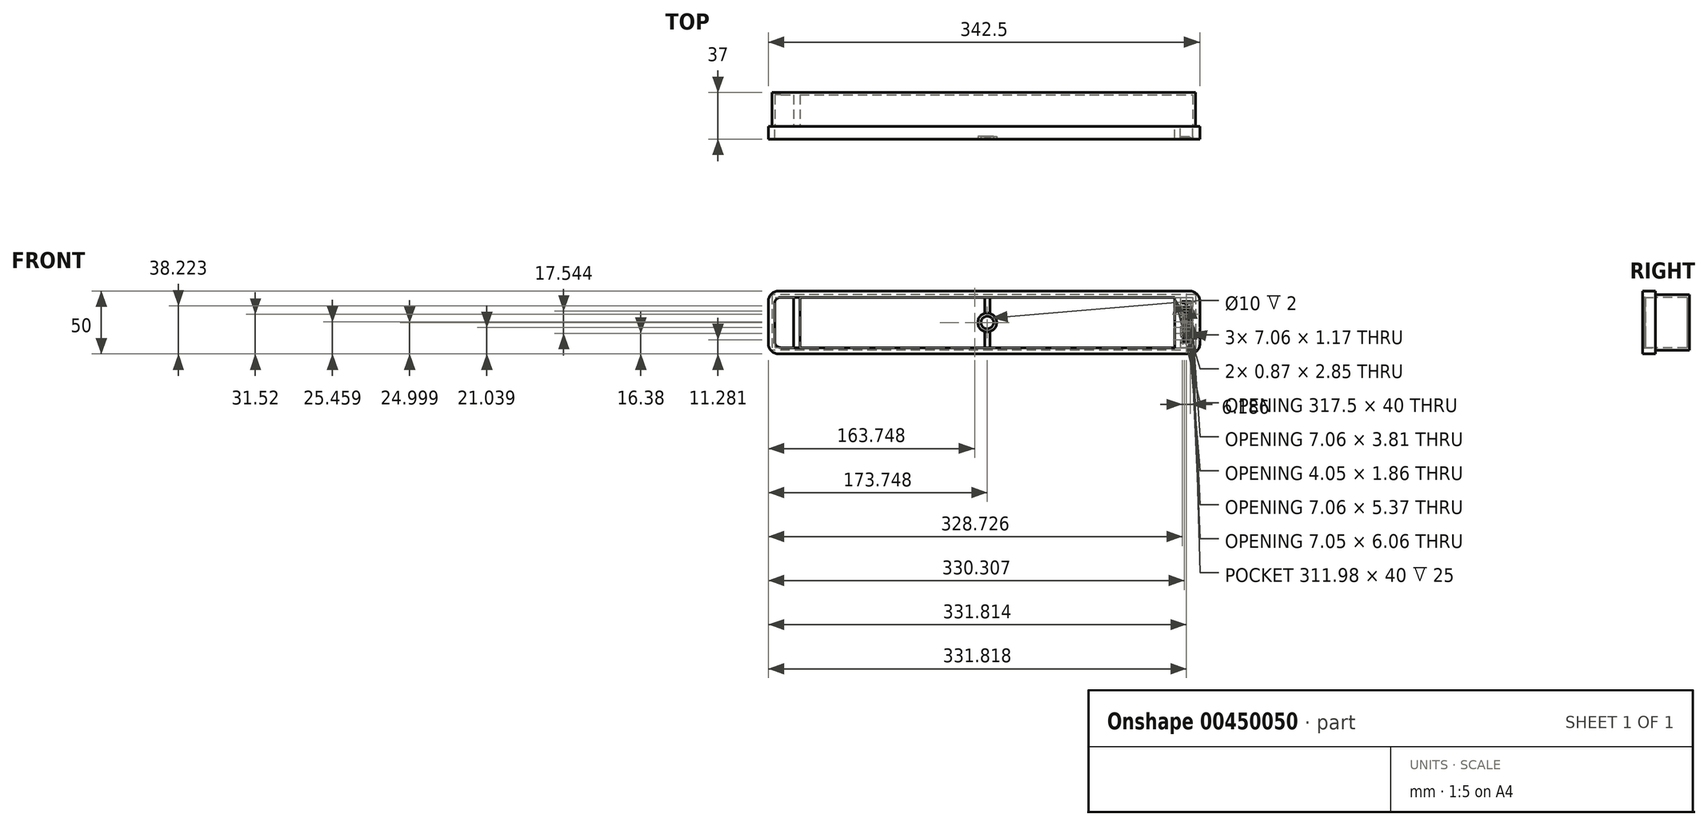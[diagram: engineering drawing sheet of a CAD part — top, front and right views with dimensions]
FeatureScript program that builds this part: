
annotation { "Feature Type Name" : "Feature", "Feature Type Description" : "" }
export const myFeature = defineFeature(function(context is Context, id is Id, definition is map)
    precondition{}
    {
        {
            var Q0;
            Q0=qCreatedBy(makeId("Front.planeOp"),FACE);
            var sketch = newSketch(context, id + "F0", { "sketchPlane" : qUnion([Q0])});
            skLineSegment(sketch, "E0.bottom", {"start": v(-305.43, 21.95) * mm, "end": v(20.67, 21.95) * mm});
            skLineSegment(sketch, "E0.top", {"start": v(-305.43, -28.05) * mm, "end": v(20.67, -28.05) * mm});
            skLineSegment(sketch, "E0.left", {"start": v(-313.63, 13.75) * mm, "end": v(-313.63, -19.85) * mm});
            skLineSegment(sketch, "E0.right", {"start": v(28.87, 13.75) * mm, "end": v(28.87, -19.85) * mm});
            skLineSegment(sketch, "E1.bottom", {"start": v(-303.63, 16.95) * mm, "end": v(8.87, 16.95) * mm});
            skLineSegment(sketch, "E1.top", {"start": v(-303.63, -23.05) * mm, "end": v(8.87, -23.05) * mm});
            skLineSegment(sketch, "E1.left", {"start": v(-308.63, 11.95) * mm, "end": v(-308.63, -18.05) * mm});
            skLineSegment(sketch, "E1.right", {"start": v(8.87, 16.95) * mm, "end": v(8.87, -23.05) * mm});
            skPoint(sketch, "E2.visualSharp", {"position": v(-308.63, 16.95) * mm});
            skArc(sketch, "E2.filletArc", {"start": v(-303.63, 16.95) * mm, "mid": v(-307.17, 15.48) * mm, "end": v(-308.63, 11.95) * mm});
            skPoint(sketch, "E3.visualSharp", {"position": v(-308.63, -23.05) * mm});
            skArc(sketch, "E3.filletArc", {"start": v(-308.63, -18.05) * mm, "mid": v(-307.17, -21.59) * mm, "end": v(-303.63, -23.05) * mm});
            skPoint(sketch, "E4.visualSharp", {"position": v(-313.63, -28.05) * mm});
            skArc(sketch, "E4.filletArc", {"start": v(-313.63, -19.85) * mm, "mid": v(-311.23, -25.65) * mm, "end": v(-305.43, -28.05) * mm});
            skPoint(sketch, "E5.visualSharp", {"position": v(-313.63, 21.95) * mm});
            skArc(sketch, "E5.filletArc", {"start": v(-305.43, 21.95) * mm, "mid": v(-311.23, 19.55) * mm, "end": v(-313.63, 13.75) * mm});
            skPoint(sketch, "E6.visualSharp", {"position": v(28.87, 21.95) * mm});
            skArc(sketch, "E6.filletArc", {"start": v(28.87, 13.75) * mm, "mid": v(26.47, 19.55) * mm, "end": v(20.67, 21.95) * mm});
            skPoint(sketch, "E7.visualSharp", {"position": v(28.87, -28.05) * mm});
            skArc(sketch, "E7.filletArc", {"start": v(20.67, -28.05) * mm, "mid": v(26.47, -25.65) * mm, "end": v(28.87, -19.85) * mm});
            skLineSegment(sketch, "E8.bottom", {"start": v(-293.63, 16.95) * mm, "end": v(-288.63, 16.95) * mm});
            skLineSegment(sketch, "E8.top", {"start": v(-293.63, -23.05) * mm, "end": v(-288.63, -23.05) * mm});
            skLineSegment(sketch, "E8.left", {"start": v(-293.63, 16.95) * mm, "end": v(-293.63, -23.05) * mm});
            skLineSegment(sketch, "E8.right", {"start": v(-288.63, 16.95) * mm, "end": v(-288.63, -23.05) * mm});
            skSolve(sketch);
        }
        {
            var Q0;
            Q0=makeQuery(id+"F0.imprint","IMPRINT",FACE,{"disambiguationData":[TD([[makeQuery(id+"F0.imprint","IMPRINT",EDGE,{"derivedFrom":sQuery(id+"F0.wireOp",EDGE,"E0.bottom")}),-1.0]])]});
            var Q1;
            Q1=makeQuery(id+"F0.imprint","IMPRINT",FACE,{"disambiguationData":[TD([[makeQuery(id+"F0.imprint","IMPRINT",EDGE,{"derivedFrom":sQuery(id+"F0.wireOp",EDGE,"E8.bottom")}),-1.0]])]});
            extrude(context, id + "F1", {"entities" : qUnion([Q0, Q1]), "depth" : 10 * mm});
        }
        {
            var Q0;
            Q0=makeQuery(id+"F1.opExtrude","CAP_FACE",FACE,{"disambiguationData":[OSD([sQuery(id+"F0.wireOp",EDGE,"E0.bottom"),sQuery(id+"F0.wireOp",EDGE,"E0.top"),sQuery(id+"F0.wireOp",EDGE,"E0.left"),sQuery(id+"F0.wireOp",EDGE,"E0.right"),sQuery(id+"F0.wireOp",EDGE,"E1.bottom"),sQuery(id+"F0.wireOp",EDGE,"E1.top"),sQuery(id+"F0.wireOp",EDGE,"E1.left"),sQuery(id+"F0.wireOp",EDGE,"E1.right"),sQuery(id+"F0.wireOp",EDGE,"zvlTqXnN-NSDQ-JKbX-Zw8z-ZxoE4PYBJVqr.bottom"),sQuery(id+"F0.wireOp",EDGE,"zvlTqXnN-NSDQ-JKbX-Zw8z-ZxoE4PYBJVqr.top"),sQuery(id+"F0.wireOp",EDGE,"zvlTqXnN-NSDQ-JKbX-Zw8z-ZxoE4PYBJVqr.left"),sQuery(id+"F0.wireOp",EDGE,"zvlTqXnN-NSDQ-JKbX-Zw8z-ZxoE4PYBJVqr.right"),sQuery(id+"F0.wireOp",EDGE,"uq8vt4s5-scxk-EfTv-IjQb-mOJCmNg2LhQu.bottom"),sQuery(id+"F0.wireOp",EDGE,"uq8vt4s5-scxk-EfTv-IjQb-mOJCmNg2LhQu.top"),sQuery(id+"F0.wireOp",EDGE,"uq8vt4s5-scxk-EfTv-IjQb-mOJCmNg2LhQu.left"),sQuery(id+"F0.wireOp",EDGE,"uq8vt4s5-scxk-EfTv-IjQb-mOJCmNg2LhQu.right"),sQuery(id+"F0.wireOp",EDGE,"y3TFfong-PjZo-lhFq-87m7-LgytcNZYgRy1.bottom"),sQuery(id+"F0.wireOp",EDGE,"y3TFfong-PjZo-lhFq-87m7-LgytcNZYgRy1.top"),sQuery(id+"F0.wireOp",EDGE,"y3TFfong-PjZo-lhFq-87m7-LgytcNZYgRy1.left"),sQuery(id+"F0.wireOp",EDGE,"y3TFfong-PjZo-lhFq-87m7-LgytcNZYgRy1.right"),sQuery(id+"F0.wireOp",EDGE,"Yr4FkV4U-5VVj-icSQ-0UOe-qvVzSsorRwRa.bottom"),sQuery(id+"F0.wireOp",EDGE,"Yr4FkV4U-5VVj-icSQ-0UOe-qvVzSsorRwRa.top"),sQuery(id+"F0.wireOp",EDGE,"Yr4FkV4U-5VVj-icSQ-0UOe-qvVzSsorRwRa.left"),sQuery(id+"F0.wireOp",EDGE,"Yr4FkV4U-5VVj-icSQ-0UOe-qvVzSsorRwRa.right")])],"isStart":false});
            var sketch = newSketch(context, id + "F2", { "sketchPlane" : qUnion([Q0])});
            skText(sketch, "E9", { "text": "HESTIA", "fontName": "AllertaStencil-Regular.ttf"});
            const initialGuessF2  = {"E9": [0.01466, 0.01454, 0, -1, 0.00706]};
            skSetInitialGuess(sketch, initialGuessF2);
            skSolve(sketch);
        }
        {
            var Q0;
            Q0 = qSketchRegion(id + "F2", true);
            extrude(context, id + "F3", {"entities" : qUnion([Q0]), "operationType" : NewBodyOperationType.REMOVE, "oppositeDirection" : true, "depth" : 5 * mm});
        }
        {
            var Q0;
            Q0=makeQuery(id+"F1.opExtrude","CAP_FACE",FACE,{"disambiguationData":[OSD([sQuery(id+"F0.wireOp",EDGE,"E0.bottom"),sQuery(id+"F0.wireOp",EDGE,"E0.top"),sQuery(id+"F0.wireOp",EDGE,"E0.left"),sQuery(id+"F0.wireOp",EDGE,"E0.right"),sQuery(id+"F0.wireOp",EDGE,"E1.bottom"),sQuery(id+"F0.wireOp",EDGE,"E1.top"),sQuery(id+"F0.wireOp",EDGE,"E1.left"),sQuery(id+"F0.wireOp",EDGE,"E1.right"),sQuery(id+"F0.wireOp",EDGE,"E2.filletArc"),sQuery(id+"F0.wireOp",EDGE,"E3.filletArc"),sQuery(id+"F0.wireOp",EDGE,"E4.filletArc"),sQuery(id+"F0.wireOp",EDGE,"E5.filletArc"),sQuery(id+"F0.wireOp",EDGE,"E6.filletArc"),sQuery(id+"F0.wireOp",EDGE,"E7.filletArc"),sQuery(id+"F0.wireOp",EDGE,"E8.left"),sQuery(id+"F0.wireOp",EDGE,"E8.right")])],"isStart":false});
            var sketch = newSketch(context, id + "F4", { "sketchPlane" : qUnion([Q0])});
            skCircle(sketch, "E10", {"center": v(-139.88, -3.05) * mm, "radius": 5 * mm});
            skPoint(sketch, "E10.centerSnap0", {"position": v(-288.63, -3.05) * mm});
            skLineSegment(sketch, "E11", {"start": v(-288.63, -3.05) * mm, "end": v(8.87, -3.05) * mm, "construction": true});
            skCircle(sketch, "E12", {"center": v(-139.88, -3.05) * mm, "radius": 7.5 * mm});
            skSolve(sketch);
        }
        {
            var Q0;
            Q0=makeQuery(id+"F4.imprint","IMPRINT",FACE,{"disambiguationData":[TD([[makeQuery(id+"F4.imprint","IMPRINT",EDGE,{"derivedFrom":sQuery(id+"F4.wireOp",EDGE,"E10")}),-1.0]])]});
            extrude(context, id + "F5", {"entities" : qUnion([Q0]), "operationType" : NewBodyOperationType.ADD, "oppositeDirection" : true, "depth" : 2 * mm});
        }
        {
            var Q0;
            Q0=makeQuery(id+"F5.opExtrude","CAP_FACE",FACE,{"disambiguationData":[OSD([sQuery(id+"F4.wireOp",EDGE,"E10"),sQuery(id+"F4.wireOp",EDGE,"E12")])],"isStart":false});
            var sketch = newSketch(context, id + "F6", { "sketchPlane" : qUnion([Q0])});
            skLineSegment(sketch, "E13.bottom", {"start": v(141.89, -8.94) * mm, "end": v(137.72, -8.94) * mm});
            skLineSegment(sketch, "E13.top", {"start": v(141.89, -23.04) * mm, "end": v(137.72, -23.04) * mm});
            skLineSegment(sketch, "E13.left", {"start": v(141.89, -8.94) * mm, "end": v(141.89, -23.04) * mm});
            skLineSegment(sketch, "E13.right", {"start": v(137.72, -8.94) * mm, "end": v(137.72, -23.04) * mm});
            skLineSegment(sketch, "E14.bottom", {"start": v(141.89, 3.14) * mm, "end": v(137.72, 3.14) * mm});
            skLineSegment(sketch, "E14.top", {"start": v(141.89, 16.95) * mm, "end": v(137.72, 16.95) * mm});
            skLineSegment(sketch, "E14.left", {"start": v(141.89, 3.14) * mm, "end": v(141.89, 16.95) * mm});
            skLineSegment(sketch, "E14.right", {"start": v(137.72, 3.14) * mm, "end": v(137.72, 16.95) * mm});
            skSolve(sketch);
        }
        {
            var Q0;
            {var subQ0=sQuery(id+"F6.wireOp",EDGE,"E14.top");Q0=makeQuery(id+"F6.imprint","IMPRINT",FACE,{"disambiguationData":[TD([[makeQuery(id+"F6.imprint","IMPRINT",EDGE,{"derivedFrom":subQ0}),1.0]])]});}
            var Q1;
            {var subQ0=sQuery(id+"F6.wireOp",EDGE,"E14.bottom");Q1=makeQuery(id+"F6.imprint","IMPRINT",FACE,{"disambiguationData":[TD([[makeQuery(id+"F6.imprint","IMPRINT",EDGE,{"derivedFrom":subQ0}),-1.0]])]});}
            var Q2;
            {var subQ0=sQuery(id+"F6.wireOp",EDGE,"E13.bottom");Q2=makeQuery(id+"F6.imprint","IMPRINT",FACE,{"disambiguationData":[TD([[makeQuery(id+"F6.imprint","IMPRINT",EDGE,{"derivedFrom":subQ0}),1.0]])]});}
            var Q3;
            {var subQ0=sQuery(id+"F6.wireOp",EDGE,"E13.top");Q3=makeQuery(id+"F6.imprint","IMPRINT",FACE,{"disambiguationData":[TD([[makeQuery(id+"F6.imprint","IMPRINT",EDGE,{"derivedFrom":subQ0}),-1.0]])]});}
            extrude(context, id + "F7", {"entities" : qUnion([Q0, Q1, Q2, Q3]), "operationType" : NewBodyOperationType.ADD, "oppositeDirection" : true, "depth" : 1 * mm});
        }
        {
            var Q0;
            Q0=makeQuery(id+"F1.opExtrude","CAP_FACE",FACE,{"disambiguationData":[OSD([sQuery(id+"F0.wireOp",EDGE,"E0.bottom"),sQuery(id+"F0.wireOp",EDGE,"E0.top"),sQuery(id+"F0.wireOp",EDGE,"E0.left"),sQuery(id+"F0.wireOp",EDGE,"E0.right"),sQuery(id+"F0.wireOp",EDGE,"E1.bottom"),sQuery(id+"F0.wireOp",EDGE,"E1.top"),sQuery(id+"F0.wireOp",EDGE,"E1.left"),sQuery(id+"F0.wireOp",EDGE,"E1.right"),sQuery(id+"F0.wireOp",EDGE,"E2.filletArc"),sQuery(id+"F0.wireOp",EDGE,"E3.filletArc"),sQuery(id+"F0.wireOp",EDGE,"E4.filletArc"),sQuery(id+"F0.wireOp",EDGE,"E5.filletArc"),sQuery(id+"F0.wireOp",EDGE,"E6.filletArc"),sQuery(id+"F0.wireOp",EDGE,"E7.filletArc"),sQuery(id+"F0.wireOp",EDGE,"E8.left"),sQuery(id+"F0.wireOp",EDGE,"E8.right")])],"isStart":true});
            var sketch = newSketch(context, id + "F8", { "sketchPlane" : qUnion([Q0])});
            skLineSegment(sketch, "E15.bottom", {"start": v(-13.33, 16.95) * mm, "end": v(-23.35, 16.95) * mm});
            skLineSegment(sketch, "E15.top", {"start": v(-13.33, -22.98) * mm, "end": v(-23.35, -22.98) * mm});
            skLineSegment(sketch, "E15.left", {"start": v(-13.33, 16.95) * mm, "end": v(-13.33, -22.98) * mm});
            skLineSegment(sketch, "E15.right", {"start": v(-23.35, 16.95) * mm, "end": v(-23.35, -22.98) * mm});
            skSolve(sketch);
        }
        {
            var Q0;
            Q0=makeQuery(id+"F8.imprint","IMPRINT",FACE,{"disambiguationData":[TD([[makeQuery(id+"F8.imprint","IMPRINT",EDGE,{"derivedFrom":sQuery(id+"F8.wireOp",EDGE,"E15.bottom")}),1.0]])]});
            extrude(context, id + "F9", {"entities" : qUnion([Q0]), "operationType" : NewBodyOperationType.REMOVE, "oppositeDirection" : true, "depth" : 9 * mm});
        }
        {
            var Q0;
            Q0=makeQuery(id+"F9.boolean.opBoolean","COPY",FACE,{"derivedFrom":makeQuery(id+"F9.opExtrude","CAP_FACE",FACE,{"disambiguationData":[OSD([sQuery(id+"F8.wireOp",EDGE,"E15.bottom"),sQuery(id+"F8.wireOp",EDGE,"E15.top"),sQuery(id+"F8.wireOp",EDGE,"E15.left"),sQuery(id+"F8.wireOp",EDGE,"E15.right")])],"isStart":false})});
            var sketch = newSketch(context, id + "F10", { "sketchPlane" : qUnion([Q0])});
            skLineSegment(sketch, "E16.bottom", {"start": v(-23.35, 16.95) * mm, "end": v(-13.33, 16.95) * mm});
            skLineSegment(sketch, "E16.top", {"start": v(-23.35, -22.98) * mm, "end": v(-13.33, -22.98) * mm});
            skLineSegment(sketch, "E16.left", {"start": v(-23.35, 16.95) * mm, "end": v(-23.35, -22.98) * mm});
            skLineSegment(sketch, "E16.right", {"start": v(-13.33, 16.95) * mm, "end": v(-13.33, -22.98) * mm});
            skSolve(sketch);
        }
        {
            var Q0;
            Q0=makeQuery(id+"F10.imprint","IMPRINT",FACE,{"disambiguationData":[TD([[makeQuery(id+"F10.imprint","IMPRINT",EDGE,{"derivedFrom":sQuery(id+"F10.wireOp",EDGE,"E16.bottom")}),1.0]])]});
            var Q1;
            {var subQ0=makeQuery(id+"F9.opExtrude","CAP_FACE",FACE,{"disambiguationData":[OSD([sQuery(id+"F8.wireOp",EDGE,"E15.bottom"),sQuery(id+"F8.wireOp",EDGE,"E15.top"),sQuery(id+"F8.wireOp",EDGE,"E15.left"),sQuery(id+"F8.wireOp",EDGE,"E15.right")])],"isStart":false});Q1=makeQuery(id+"F10.imprint","IMPRINT",FACE,{"disambiguationData":[TD([[makeQuery(id+"F10.imprint","IMPRINT",EDGE,{"derivedFrom":makeQuery(id+"F9.boolean.opBoolean","INTERSECT",EDGE,{"derivedFrom":[makeQuery(id+"F3.boolean.opBoolean","COPY",FACE,{"derivedFrom":makeQuery(id+"F3.opExtrude","SWEPT_FACE",FACE,{"disambiguationData":[OSD([sQuery(id+"F2.wireOp",EDGE,"E9.sketch_text.stroke-8")])]})}),subQ0]})}),1.0]])]});}
            var Q2;
            {var subQ0=makeQuery(id+"F9.opExtrude","CAP_FACE",FACE,{"disambiguationData":[OSD([sQuery(id+"F8.wireOp",EDGE,"E15.bottom"),sQuery(id+"F8.wireOp",EDGE,"E15.top"),sQuery(id+"F8.wireOp",EDGE,"E15.left"),sQuery(id+"F8.wireOp",EDGE,"E15.right")])],"isStart":false});Q2=makeQuery(id+"F10.imprint","IMPRINT",FACE,{"disambiguationData":[TD([[makeQuery(id+"F10.imprint","IMPRINT",EDGE,{"derivedFrom":makeQuery(id+"F9.boolean.opBoolean","INTERSECT",EDGE,{"derivedFrom":[makeQuery(id+"F3.boolean.opBoolean","COPY",FACE,{"derivedFrom":makeQuery(id+"F3.opExtrude","SWEPT_FACE",FACE,{"disambiguationData":[OSD([sQuery(id+"F2.wireOp",EDGE,"E9.sketch_text.stroke-0")])]})}),subQ0]})}),1.0]])]});}
            var Q3;
            {var subQ0=makeQuery(id+"F9.opExtrude","CAP_FACE",FACE,{"disambiguationData":[OSD([sQuery(id+"F8.wireOp",EDGE,"E15.bottom"),sQuery(id+"F8.wireOp",EDGE,"E15.top"),sQuery(id+"F8.wireOp",EDGE,"E15.left"),sQuery(id+"F8.wireOp",EDGE,"E15.right")])],"isStart":false});Q3=makeQuery(id+"F10.imprint","IMPRINT",FACE,{"disambiguationData":[TD([[makeQuery(id+"F10.imprint","IMPRINT",EDGE,{"derivedFrom":makeQuery(id+"F9.boolean.opBoolean","INTERSECT",EDGE,{"derivedFrom":[makeQuery(id+"F3.boolean.opBoolean","COPY",FACE,{"derivedFrom":makeQuery(id+"F3.opExtrude","SWEPT_FACE",FACE,{"disambiguationData":[OSD([sQuery(id+"F2.wireOp",EDGE,"E9.sketch_text.stroke-12")])]})}),subQ0]})}),1.0]])]});}
            var Q4;
            {var subQ0=makeQuery(id+"F9.opExtrude","CAP_FACE",FACE,{"disambiguationData":[OSD([sQuery(id+"F8.wireOp",EDGE,"E15.bottom"),sQuery(id+"F8.wireOp",EDGE,"E15.top"),sQuery(id+"F8.wireOp",EDGE,"E15.left"),sQuery(id+"F8.wireOp",EDGE,"E15.right")])],"isStart":false});Q4=makeQuery(id+"F10.imprint","IMPRINT",FACE,{"disambiguationData":[TD([[makeQuery(id+"F10.imprint","IMPRINT",EDGE,{"derivedFrom":makeQuery(id+"F9.boolean.opBoolean","INTERSECT",EDGE,{"derivedFrom":[makeQuery(id+"F3.boolean.opBoolean","COPY",FACE,{"derivedFrom":makeQuery(id+"F3.opExtrude","SWEPT_FACE",FACE,{"disambiguationData":[OSD([sQuery(id+"F2.wireOp",EDGE,"E9.sketch_text.stroke-24")])]})}),subQ0]})}),1.0]])]});}
            var Q5;
            {var subQ0=makeQuery(id+"F9.opExtrude","CAP_FACE",FACE,{"disambiguationData":[OSD([sQuery(id+"F8.wireOp",EDGE,"E15.bottom"),sQuery(id+"F8.wireOp",EDGE,"E15.top"),sQuery(id+"F8.wireOp",EDGE,"E15.left"),sQuery(id+"F8.wireOp",EDGE,"E15.right")])],"isStart":false});Q5=makeQuery(id+"F10.imprint","IMPRINT",FACE,{"disambiguationData":[TD([[makeQuery(id+"F10.imprint","IMPRINT",EDGE,{"derivedFrom":makeQuery(id+"F9.boolean.opBoolean","INTERSECT",EDGE,{"derivedFrom":[makeQuery(id+"F3.boolean.opBoolean","COPY",FACE,{"derivedFrom":makeQuery(id+"F3.opExtrude","SWEPT_FACE",FACE,{"disambiguationData":[OSD([sQuery(id+"F2.wireOp",EDGE,"E9.sketch_text.stroke-16")])]})}),subQ0]})}),1.0]])]});}
            var Q6;
            {var subQ0=makeQuery(id+"F9.opExtrude","CAP_FACE",FACE,{"disambiguationData":[OSD([sQuery(id+"F8.wireOp",EDGE,"E15.bottom"),sQuery(id+"F8.wireOp",EDGE,"E15.top"),sQuery(id+"F8.wireOp",EDGE,"E15.left"),sQuery(id+"F8.wireOp",EDGE,"E15.right")])],"isStart":false});Q6=makeQuery(id+"F10.imprint","IMPRINT",FACE,{"disambiguationData":[TD([[makeQuery(id+"F10.imprint","IMPRINT",EDGE,{"derivedFrom":makeQuery(id+"F9.boolean.opBoolean","INTERSECT",EDGE,{"derivedFrom":[makeQuery(id+"F3.boolean.opBoolean","COPY",FACE,{"derivedFrom":makeQuery(id+"F3.opExtrude","SWEPT_FACE",FACE,{"disambiguationData":[OSD([sQuery(id+"F2.wireOp",EDGE,"E9.sketch_text.stroke-20")])]})}),subQ0]})}),1.0]])]});}
            var Q7;
            {var subQ0=makeQuery(id+"F9.opExtrude","CAP_FACE",FACE,{"disambiguationData":[OSD([sQuery(id+"F8.wireOp",EDGE,"E15.bottom"),sQuery(id+"F8.wireOp",EDGE,"E15.top"),sQuery(id+"F8.wireOp",EDGE,"E15.left"),sQuery(id+"F8.wireOp",EDGE,"E15.right")])],"isStart":false});Q7=makeQuery(id+"F10.imprint","IMPRINT",FACE,{"disambiguationData":[TD([[makeQuery(id+"F10.imprint","IMPRINT",EDGE,{"derivedFrom":makeQuery(id+"F9.boolean.opBoolean","INTERSECT",EDGE,{"derivedFrom":[makeQuery(id+"F3.boolean.opBoolean","COPY",FACE,{"derivedFrom":makeQuery(id+"F3.opExtrude","SWEPT_FACE",FACE,{"disambiguationData":[OSD([sQuery(id+"F2.wireOp",EDGE,"E9.sketch_text.stroke-65")])]})}),subQ0]})}),1.0]])]});}
            var Q8;
            {var subQ0=makeQuery(id+"F9.opExtrude","CAP_FACE",FACE,{"disambiguationData":[OSD([sQuery(id+"F8.wireOp",EDGE,"E15.bottom"),sQuery(id+"F8.wireOp",EDGE,"E15.top"),sQuery(id+"F8.wireOp",EDGE,"E15.left"),sQuery(id+"F8.wireOp",EDGE,"E15.right")])],"isStart":false});Q8=makeQuery(id+"F10.imprint","IMPRINT",FACE,{"disambiguationData":[TD([[makeQuery(id+"F10.imprint","IMPRINT",EDGE,{"derivedFrom":makeQuery(id+"F9.boolean.opBoolean","INTERSECT",EDGE,{"derivedFrom":[makeQuery(id+"F3.boolean.opBoolean","COPY",FACE,{"derivedFrom":makeQuery(id+"F3.opExtrude","SWEPT_FACE",FACE,{"disambiguationData":[OSD([sQuery(id+"F2.wireOp",EDGE,"E9.sketch_text.stroke-53")])]})}),subQ0]})}),1.0]])]});}
            var Q9;
            {var subQ0=makeQuery(id+"F9.opExtrude","CAP_FACE",FACE,{"disambiguationData":[OSD([sQuery(id+"F8.wireOp",EDGE,"E15.bottom"),sQuery(id+"F8.wireOp",EDGE,"E15.top"),sQuery(id+"F8.wireOp",EDGE,"E15.left"),sQuery(id+"F8.wireOp",EDGE,"E15.right")])],"isStart":false});Q9=makeQuery(id+"F10.imprint","IMPRINT",FACE,{"disambiguationData":[TD([[makeQuery(id+"F10.imprint","IMPRINT",EDGE,{"derivedFrom":makeQuery(id+"F9.boolean.opBoolean","INTERSECT",EDGE,{"derivedFrom":[makeQuery(id+"F3.boolean.opBoolean","COPY",FACE,{"derivedFrom":makeQuery(id+"F3.opExtrude","SWEPT_FACE",FACE,{"disambiguationData":[OSD([sQuery(id+"F2.wireOp",EDGE,"E9.sketch_text.stroke-39")])]})}),subQ0]})}),1.0]])]});}
            var Q10;
            {var subQ0=makeQuery(id+"F9.opExtrude","CAP_FACE",FACE,{"disambiguationData":[OSD([sQuery(id+"F8.wireOp",EDGE,"E15.bottom"),sQuery(id+"F8.wireOp",EDGE,"E15.top"),sQuery(id+"F8.wireOp",EDGE,"E15.left"),sQuery(id+"F8.wireOp",EDGE,"E15.right")])],"isStart":false});Q10=makeQuery(id+"F10.imprint","IMPRINT",FACE,{"disambiguationData":[TD([[makeQuery(id+"F10.imprint","IMPRINT",EDGE,{"derivedFrom":makeQuery(id+"F9.boolean.opBoolean","INTERSECT",EDGE,{"derivedFrom":[makeQuery(id+"F3.boolean.opBoolean","COPY",FACE,{"derivedFrom":makeQuery(id+"F3.opExtrude","SWEPT_FACE",FACE,{"disambiguationData":[OSD([sQuery(id+"F2.wireOp",EDGE,"E9.sketch_text.stroke-28")])]})}),subQ0]})}),1.0]])]});}
            var Q11;
            {var subQ0=makeQuery(id+"F9.opExtrude","CAP_FACE",FACE,{"disambiguationData":[OSD([sQuery(id+"F8.wireOp",EDGE,"E15.bottom"),sQuery(id+"F8.wireOp",EDGE,"E15.top"),sQuery(id+"F8.wireOp",EDGE,"E15.left"),sQuery(id+"F8.wireOp",EDGE,"E15.right")])],"isStart":false});Q11=makeQuery(id+"F10.imprint","IMPRINT",FACE,{"disambiguationData":[TD([[makeQuery(id+"F10.imprint","IMPRINT",EDGE,{"derivedFrom":makeQuery(id+"F9.boolean.opBoolean","INTERSECT",EDGE,{"derivedFrom":[makeQuery(id+"F3.boolean.opBoolean","COPY",FACE,{"derivedFrom":makeQuery(id+"F3.opExtrude","SWEPT_FACE",FACE,{"disambiguationData":[OSD([sQuery(id+"F2.wireOp",EDGE,"E9.sketch_text.stroke-78")])]})}),subQ0]})}),1.0]])]});}
            var Q12;
            {var subQ0=makeQuery(id+"F9.opExtrude","CAP_FACE",FACE,{"disambiguationData":[OSD([sQuery(id+"F8.wireOp",EDGE,"E15.bottom"),sQuery(id+"F8.wireOp",EDGE,"E15.top"),sQuery(id+"F8.wireOp",EDGE,"E15.left"),sQuery(id+"F8.wireOp",EDGE,"E15.right")])],"isStart":false});Q12=makeQuery(id+"F10.imprint","IMPRINT",FACE,{"disambiguationData":[TD([[makeQuery(id+"F10.imprint","IMPRINT",EDGE,{"derivedFrom":makeQuery(id+"F9.boolean.opBoolean","INTERSECT",EDGE,{"derivedFrom":[makeQuery(id+"F3.boolean.opBoolean","COPY",FACE,{"derivedFrom":makeQuery(id+"F3.opExtrude","SWEPT_FACE",FACE,{"disambiguationData":[OSD([sQuery(id+"F2.wireOp",EDGE,"E9.sketch_text.stroke-86")])]})}),subQ0]})}),1.0]])]});}
            var Q13;
            {var subQ0=makeQuery(id+"F9.opExtrude","CAP_FACE",FACE,{"disambiguationData":[OSD([sQuery(id+"F8.wireOp",EDGE,"E15.bottom"),sQuery(id+"F8.wireOp",EDGE,"E15.top"),sQuery(id+"F8.wireOp",EDGE,"E15.left"),sQuery(id+"F8.wireOp",EDGE,"E15.right")])],"isStart":false});Q13=makeQuery(id+"F10.imprint","IMPRINT",FACE,{"disambiguationData":[TD([[makeQuery(id+"F10.imprint","IMPRINT",EDGE,{"derivedFrom":makeQuery(id+"F9.boolean.opBoolean","INTERSECT",EDGE,{"derivedFrom":[makeQuery(id+"F3.boolean.opBoolean","COPY",FACE,{"derivedFrom":makeQuery(id+"F3.opExtrude","SWEPT_FACE",FACE,{"disambiguationData":[OSD([sQuery(id+"F2.wireOp",EDGE,"E9.sketch_text.stroke-90")])]})}),subQ0]})}),1.0]])]});}
            var Q14;
            {var subQ0=makeQuery(id+"F9.opExtrude","CAP_FACE",FACE,{"disambiguationData":[OSD([sQuery(id+"F8.wireOp",EDGE,"E15.bottom"),sQuery(id+"F8.wireOp",EDGE,"E15.top"),sQuery(id+"F8.wireOp",EDGE,"E15.left"),sQuery(id+"F8.wireOp",EDGE,"E15.right")])],"isStart":false});Q14=makeQuery(id+"F10.imprint","IMPRINT",FACE,{"disambiguationData":[TD([[makeQuery(id+"F10.imprint","IMPRINT",EDGE,{"derivedFrom":makeQuery(id+"F9.boolean.opBoolean","INTERSECT",EDGE,{"derivedFrom":[makeQuery(id+"F3.boolean.opBoolean","COPY",FACE,{"derivedFrom":makeQuery(id+"F3.opExtrude","SWEPT_FACE",FACE,{"disambiguationData":[OSD([sQuery(id+"F2.wireOp",EDGE,"E9.sketch_text.stroke-97")])]})}),subQ0]})}),1.0]])]});}
            extrude(context, id + "F11", {"entities" : qUnion([Q0, Q1, Q2, Q3, Q4, Q5, Q6, Q7, Q8, Q9, Q10, Q11, Q12, Q13, Q14]), "depth" : 1 * mm});
        }
        {
            var Q0;
            Q0=makeQuery(id+"F1.opExtrude","CAP_FACE",FACE,{"disambiguationData":[OSD([sQuery(id+"F0.wireOp",EDGE,"E0.bottom"),sQuery(id+"F0.wireOp",EDGE,"E0.top"),sQuery(id+"F0.wireOp",EDGE,"E0.left"),sQuery(id+"F0.wireOp",EDGE,"E0.right"),sQuery(id+"F0.wireOp",EDGE,"E1.bottom"),sQuery(id+"F0.wireOp",EDGE,"E1.top"),sQuery(id+"F0.wireOp",EDGE,"E1.left"),sQuery(id+"F0.wireOp",EDGE,"E1.right"),sQuery(id+"F0.wireOp",EDGE,"E2.filletArc"),sQuery(id+"F0.wireOp",EDGE,"E3.filletArc"),sQuery(id+"F0.wireOp",EDGE,"E4.filletArc"),sQuery(id+"F0.wireOp",EDGE,"E5.filletArc"),sQuery(id+"F0.wireOp",EDGE,"E6.filletArc"),sQuery(id+"F0.wireOp",EDGE,"E7.filletArc"),sQuery(id+"F0.wireOp",EDGE,"E8.left"),sQuery(id+"F0.wireOp",EDGE,"E8.right")])],"isStart":true});
            var sketch = newSketch(context, id + "F12", { "sketchPlane" : qUnion([Q0])});
            skLineSegment(sketch, "E17.bottom", {"start": v(-23.35, 16.95) * mm, "end": v(303.63, 16.95) * mm});
            skLineSegment(sketch, "E17.top", {"start": v(-23.35, -23.05) * mm, "end": v(303.63, -23.05) * mm});
            skLineSegment(sketch, "E17.left", {"start": v(-23.35, 16.95) * mm, "end": v(-23.35, -23.05) * mm});
            skLineSegment(sketch, "E17.right", {"start": v(308.63, 11.95) * mm, "end": v(308.63, -18.05) * mm});
            skLineSegment(sketch, "E18.bottom", {"start": v(-25.35, 18.95) * mm, "end": v(310.63, 18.95) * mm});
            skLineSegment(sketch, "E18.top", {"start": v(-25.35, -25.05) * mm, "end": v(310.63, -25.05) * mm});
            skLineSegment(sketch, "E18.left", {"start": v(-25.35, 18.95) * mm, "end": v(-25.35, -25.05) * mm});
            skLineSegment(sketch, "E18.right", {"start": v(310.63, 18.95) * mm, "end": v(310.63, -25.05) * mm});
            skLineSegment(sketch, "E19", {"start": v(288.63, 16.95) * mm, "end": v(288.63, -23.05) * mm});
            skLineSegment(sketch, "E20", {"start": v(293.63, 16.95) * mm, "end": v(293.63, -23.05) * mm});
            skPoint(sketch, "E21.visualSharp", {"position": v(308.63, 16.95) * mm});
            skArc(sketch, "E21.filletArc", {"start": v(308.63, 11.95) * mm, "mid": v(307.17, 15.48) * mm, "end": v(303.63, 16.95) * mm});
            skPoint(sketch, "E22.visualSharp", {"position": v(308.63, -23.05) * mm});
            skArc(sketch, "E22.filletArc", {"start": v(303.63, -23.05) * mm, "mid": v(307.17, -21.59) * mm, "end": v(308.63, -18.05) * mm});
            skSolve(sketch);
        }
        {
            var Q0;
            Q0=makeQuery(id+"F12.imprint","IMPRINT",FACE,{"disambiguationData":[TD([[makeQuery(id+"F12.imprint","IMPRINT",EDGE,{"derivedFrom":sQuery(id+"F12.wireOp",EDGE,"E18.bottom")}),-1.0]])]});
            var Q1;
            {var subQ2=sQuery(id+"F12.wireOp",EDGE,"E19");Q1=makeQuery(id+"F12.imprint","IMPRINT",FACE,{"disambiguationData":[TD([[makeQuery(id+"F12.imprint","IMPRINT",EDGE,{"derivedFrom":subQ2}),1.0]])]});}
            extrude(context, id + "F13", {"entities" : qUnion([Q0, Q1]), "depth" : 25 * mm});
        }
        {
            var Q0;
            Q0=makeQuery(id+"F13.opExtrude","CAP_FACE",FACE,{"disambiguationData":[OSD([sQuery(id+"F12.wireOp",EDGE,"E17.bottom"),sQuery(id+"F12.wireOp",EDGE,"E17.top"),sQuery(id+"F12.wireOp",EDGE,"E17.left"),sQuery(id+"F12.wireOp",EDGE,"E17.right"),sQuery(id+"F12.wireOp",EDGE,"E18.bottom"),sQuery(id+"F12.wireOp",EDGE,"E18.top"),sQuery(id+"F12.wireOp",EDGE,"E18.left"),sQuery(id+"F12.wireOp",EDGE,"E18.right"),sQuery(id+"F12.wireOp",EDGE,"E19"),sQuery(id+"F12.wireOp",EDGE,"E20"),sQuery(id+"F12.wireOp",EDGE,"E21.filletArc"),sQuery(id+"F12.wireOp",EDGE,"E22.filletArc")])],"isStart":false});
            var sketch = newSketch(context, id + "F14", { "sketchPlane" : qUnion([Q0])});
            skLineSegment(sketch, "E23.bottom", {"start": v(-25.35, 18.95) * mm, "end": v(310.63, 18.95) * mm});
            skLineSegment(sketch, "E23.top", {"start": v(-25.35, -25.05) * mm, "end": v(310.63, -25.05) * mm});
            skLineSegment(sketch, "E23.left", {"start": v(-25.35, 18.95) * mm, "end": v(-25.35, -25.05) * mm});
            skLineSegment(sketch, "E23.right", {"start": v(310.63, 18.95) * mm, "end": v(310.63, -25.05) * mm});
            skSolve(sketch);
        }
        {
            var Q0;
            Q0 = qSketchRegion(id + "F14", true);
            extrude(context, id + "F15", {"entities" : qUnion([Q0]), "operationType" : NewBodyOperationType.ADD, "depth" : 2 * mm});
        }
    });
